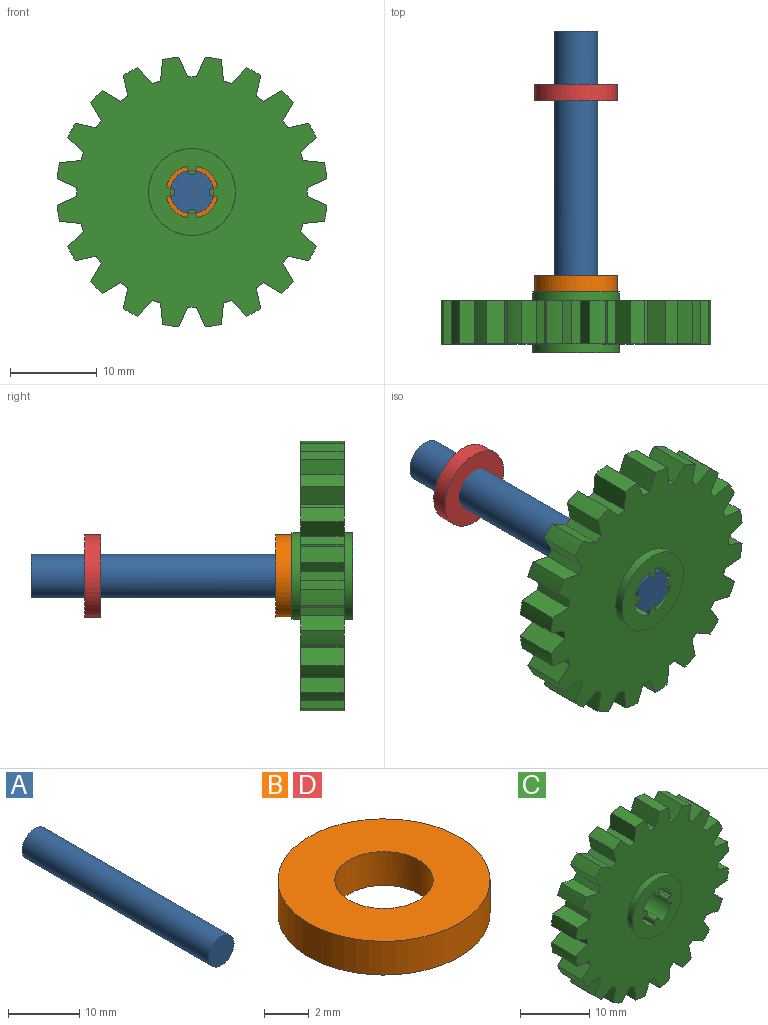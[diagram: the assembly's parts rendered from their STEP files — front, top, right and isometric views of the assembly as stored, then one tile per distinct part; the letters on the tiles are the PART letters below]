
ASSEMBLY  parts=4 mates=5
PART A: 3 faces, bbox 5x37x5 mm
  f0: plane 5x5mm, normal (0,1,0), area 19.6mm2, adj f1
  f1: cylinder r=2.5mm len=37mm, axis (0,-1,0), area 581.2mm2, adj f0,f2
  f2: plane 5x5mm, normal (0,-1,0), area 19.6mm2, adj f1
PART B: 4 faces, bbox 9.5x9.5x1.9 mm
  f0: cylinder r=2.21mm len=4.42mm, axis (0,0,1), area 25.7mm2, adj f1,f3
  f1: plane 9.53x9.53mm, normal (0,0,-1), area 55.9mm2, adj f0,f2
  f2: cylinder r=4.76mm len=9.53mm, axis (0,0,-1), area 55.5mm2, adj f1,f3
  f3: plane 9.53x9.53mm, normal (0,0,1), area 55.9mm2, adj f0,f2
PART C: 102 faces, bbox 31.1x7x31.1 mm
  f0: plane 31.06x31.06mm, normal (0,1,0), area 593.1mm2, adj f1,f7,f8,f9,f10,f11,f12,f13
  f1: cylinder r=5mm len=10mm, axis (0,1,0), area 31.4mm2, adj f0,f2
  f2: plane 10x10mm, normal (0,1,0), area 53.8mm2, adj f1,f3,f87,f88,f89,f90,f91,f92
  f3: cylinder r=0.5mm len=7mm, axis (0,-1,0), area 11mm2, adj f2,f4,f87,f98
  f4: plane 10x10mm, normal (0,-1,0), area 53.8mm2, adj f3,f5,f87,f88,f89,f90,f91,f92
  f5: cylinder r=5mm len=10mm, axis (0,-1,0), area 31.4mm2, adj f4,f6
  f6: plane 31.06x31.06mm, normal (0,-1,0), area 593.1mm2, adj f5,f7,f8,f9,f10,f11,f12,f13
  f7: plane 5x0.95mm, normal (-0.31,0,0.95), area 5mm2, adj f0,f6,f8,f86
  f8: plane 5x2.45mm, normal (-0.99,0,0.1), area 12.3mm2, adj f0,f6,f7,f28
  f9: cylinder r=15.6mm len=5mm, axis (0,-1,0), area 9.5mm2, adj f0,f6,f29,f32
  f10: cylinder r=15.6mm len=5mm, axis (0,-1,0), area 9.5mm2, adj f0,f6,f31,f35
  f11: cylinder r=15.6mm len=5mm, axis (0,-1,0), area 9.5mm2, adj f0,f6,f37,f38
  f12: cylinder r=15.6mm len=5mm, axis (0,-1,0), area 9.5mm2, adj f0,f6,f40,f41
  f13: cylinder r=15.6mm len=5mm, axis (0,-1,0), area 9.5mm2, adj f0,f6,f43,f44
  f14: cylinder r=15.6mm len=5mm, axis (0,-1,0), area 9.5mm2, adj f0,f6,f46,f47
  f15: cylinder r=15.6mm len=5mm, axis (0,-1,0), area 9.5mm2, adj f0,f6,f49,f50
  f16: cylinder r=15.6mm len=5mm, axis (0,-1,0), area 9.5mm2, adj f0,f6,f52,f53
  f17: cylinder r=15.6mm len=5mm, axis (0,-1,0), area 9.5mm2, adj f0,f6,f55,f56
  f18: cylinder r=15.6mm len=5mm, axis (0,-1,0), area 9.5mm2, adj f0,f6,f58,f59
  f19: cylinder r=15.6mm len=5mm, axis (0,-1,0), area 9.5mm2, adj f0,f6,f61,f62
  f20: cylinder r=15.6mm len=5mm, axis (0,-1,0), area 9.5mm2, adj f0,f6,f64,f65
  f21: cylinder r=15.6mm len=5mm, axis (0,-1,0), area 9.5mm2, adj f0,f6,f67,f68
  f22: cylinder r=15.6mm len=5mm, axis (0,-1,0), area 9.5mm2, adj f0,f6,f70,f71
  f23: cylinder r=15.6mm len=5mm, axis (0,-1,0), area 9.5mm2, adj f0,f6,f73,f74
  f24: cylinder r=15.6mm len=5mm, axis (0,-1,0), area 9.5mm2, adj f0,f6,f76,f77
  f25: cylinder r=15.6mm len=5mm, axis (0,-1,0), area 9.5mm2, adj f0,f6,f79,f80
  f26: cylinder r=15.6mm len=5mm, axis (0,-1,0), area 9.5mm2, adj f0,f6,f82,f83
  f27: cylinder r=15.6mm len=5mm, axis (0,-1,0), area 9.5mm2, adj f0,f6,f85,f86
  f28: cylinder r=15.6mm len=5mm, axis (0,-1,0), area 9.5mm2, adj f0,f6,f8,f34
  f29: plane 5x2.45mm, normal (0.99,0,0.1), area 12.3mm2, adj f0,f6,f9,f30
  f30: plane 5x0.95mm, normal (0.31,0,0.95), area 5mm2, adj f0,f6,f29,f31
  f31: plane 5x1.83mm, normal (-0.74,0,0.67), area 12.3mm2, adj f0,f6,f10,f30
  f32: plane 5x2.25mm, normal (-0.91,0,0.41), area 12.3mm2, adj f0,f6,f9,f33
  f33: plane 5x1mm, normal (0,0,1), area 5mm2, adj f0,f6,f32,f34
  f34: plane 5x2.25mm, normal (0.91,0,0.41), area 12.3mm2, adj f0,f6,f28,f33
  f35: plane 5x2.41mm, normal (0.98,0,-0.21), area 12.3mm2, adj f0,f6,f10,f36
  f36: plane 5x0.81mm, normal (0.59,0,0.81), area 5mm2, adj f0,f6,f35,f37
  f37: plane 5x2.13mm, normal (-0.5,0,0.87), area 12.3mm2, adj f0,f6,f11,f36
  f38: plane 5x2.13mm, normal (0.87,0,-0.5), area 12.3mm2, adj f0,f6,f11,f39
  f39: plane 5x0.81mm, normal (0.81,0,0.59), area 5mm2, adj f0,f6,f38,f40
  f40: plane 5x2.41mm, normal (-0.21,0,0.98), area 12.3mm2, adj f0,f6,f12,f39
  f41: plane 5x1.83mm, normal (0.67,0,-0.74), area 12.3mm2, adj f0,f6,f12,f42
  f42: plane 5x0.95mm, normal (0.95,0,0.31), area 5mm2, adj f0,f6,f41,f43
  f43: plane 5x2.45mm, normal (0.1,0,0.99), area 12.3mm2, adj f0,f6,f13,f42
  f44: plane 5x2.25mm, normal (0.41,0,-0.91), area 12.3mm2, adj f0,f6,f13,f45
  f45: plane 5x1mm, normal (1,0,0), area 5mm2, adj f0,f6,f44,f46
  f46: plane 5x2.25mm, normal (0.41,0,0.91), area 12.3mm2, adj f0,f6,f14,f45
  f47: plane 5x2.45mm, normal (0.1,0,-0.99), area 12.3mm2, adj f0,f6,f14,f48
  f48: plane 5x0.95mm, normal (0.95,0,-0.31), area 5mm2, adj f0,f6,f47,f49
  f49: plane 5x1.83mm, normal (0.67,0,0.74), area 12.3mm2, adj f0,f6,f15,f48
  f50: plane 5x2.41mm, normal (-0.21,0,-0.98), area 12.3mm2, adj f0,f6,f15,f51
  f51: plane 5x0.81mm, normal (0.81,0,-0.59), area 5mm2, adj f0,f6,f50,f52
  f52: plane 5x2.13mm, normal (0.87,0,0.5), area 12.3mm2, adj f0,f6,f16,f51
  f53: plane 5x2.13mm, normal (-0.5,0,-0.87), area 12.3mm2, adj f0,f6,f16,f54
  f54: plane 5x0.81mm, normal (0.59,0,-0.81), area 5mm2, adj f0,f6,f53,f55
  f55: plane 5x2.41mm, normal (0.98,0,0.21), area 12.3mm2, adj f0,f6,f17,f54
  f56: plane 5x1.83mm, normal (-0.74,0,-0.67), area 12.3mm2, adj f0,f6,f17,f57
  f57: plane 5x0.95mm, normal (0.31,0,-0.95), area 5mm2, adj f0,f6,f56,f58
  f58: plane 5x2.45mm, normal (0.99,0,-0.1), area 12.3mm2, adj f0,f6,f18,f57
  f59: plane 5x2.25mm, normal (-0.91,0,-0.41), area 12.3mm2, adj f0,f6,f18,f60
  f60: plane 5x1mm, normal (0,0,-1), area 5mm2, adj f0,f6,f59,f61
  f61: plane 5x2.25mm, normal (0.91,0,-0.41), area 12.3mm2, adj f0,f6,f19,f60
  f62: plane 5x2.45mm, normal (-0.99,0,-0.1), area 12.3mm2, adj f0,f6,f19,f63
  f63: plane 5x0.95mm, normal (-0.31,0,-0.95), area 5mm2, adj f0,f6,f62,f64
  f64: plane 5x1.83mm, normal (0.74,0,-0.67), area 12.3mm2, adj f0,f6,f20,f63
  f65: plane 5x2.41mm, normal (-0.98,0,0.21), area 12.3mm2, adj f0,f6,f20,f66
  f66: plane 5x0.81mm, normal (-0.59,0,-0.81), area 5mm2, adj f0,f6,f65,f67
  f67: plane 5x2.13mm, normal (0.5,0,-0.87), area 12.3mm2, adj f0,f6,f21,f66
  f68: plane 5x2.13mm, normal (-0.87,0,0.5), area 12.3mm2, adj f0,f6,f21,f69
  f69: plane 5x0.81mm, normal (-0.81,0,-0.59), area 5mm2, adj f0,f6,f68,f70
  f70: plane 5x2.41mm, normal (0.21,0,-0.98), area 12.3mm2, adj f0,f6,f22,f69
  f71: plane 5x1.83mm, normal (-0.67,0,0.74), area 12.3mm2, adj f0,f6,f22,f72
  f72: plane 5x0.95mm, normal (-0.95,0,-0.31), area 5mm2, adj f0,f6,f71,f73
  f73: plane 5x2.45mm, normal (-0.1,0,-0.99), area 12.3mm2, adj f0,f6,f23,f72
  f74: plane 5x2.25mm, normal (-0.41,0,0.91), area 12.3mm2, adj f0,f6,f23,f75
  f75: plane 5x1mm, normal (-1,0,0), area 5mm2, adj f0,f6,f74,f76
  f76: plane 5x2.25mm, normal (-0.41,0,-0.91), area 12.3mm2, adj f0,f6,f24,f75
  f77: plane 5x2.45mm, normal (-0.1,0,0.99), area 12.3mm2, adj f0,f6,f24,f78
  f78: plane 5x0.95mm, normal (-0.95,0,0.31), area 5mm2, adj f0,f6,f77,f79
  f79: plane 5x1.83mm, normal (-0.67,0,-0.74), area 12.3mm2, adj f0,f6,f25,f78
  f80: plane 5x2.41mm, normal (0.21,0,0.98), area 12.3mm2, adj f0,f6,f25,f81
  f81: plane 5x0.81mm, normal (-0.81,0,0.59), area 5mm2, adj f0,f6,f80,f82
  f82: plane 5x2.13mm, normal (-0.87,0,-0.5), area 12.3mm2, adj f0,f6,f26,f81
  f83: plane 5x2.13mm, normal (0.5,0,0.87), area 12.3mm2, adj f0,f6,f26,f84
  f84: plane 5x0.81mm, normal (-0.59,0,0.81), area 5mm2, adj f0,f6,f83,f85
  f85: plane 5x2.41mm, normal (-0.98,0,-0.21), area 12.3mm2, adj f0,f6,f27,f84
  f86: plane 5x1.83mm, normal (0.74,0,0.67), area 12.3mm2, adj f0,f6,f7,f27
  f87: plane 7x0.46mm, normal (-1,0,0), area 3.2mm2, adj f2,f3,f4,f88
  f88: cylinder r=3mm len=7mm, axis (0,1,0), area 26mm2, adj f2,f4,f87,f92
  f89: cylinder r=3mm len=7mm, axis (0,1,0), area 26mm2, adj f2,f4,f95,f98
  f90: cylinder r=3mm len=7mm, axis (0,1,0), area 26mm2, adj f2,f4,f97,f99
  f91: cylinder r=3mm len=7mm, axis (0,1,0), area 26mm2, adj f2,f4,f94,f101
  f92: plane 7x0.46mm, normal (0,0,1), area 3.2mm2, adj f2,f4,f88,f93
  f93: cylinder r=0.5mm len=7mm, axis (0,-1,0), area 11mm2, adj f2,f4,f92,f94
  f94: plane 7x0.46mm, normal (0,0,-1), area 3.2mm2, adj f2,f4,f91,f93
  f95: plane 7x0.46mm, normal (0,0,1), area 3.2mm2, adj f2,f4,f89,f96
  f96: cylinder r=0.5mm len=7mm, axis (0,-1,0), area 11mm2, adj f2,f4,f95,f97
  f97: plane 7x0.46mm, normal (0,0,-1), area 3.2mm2, adj f2,f4,f90,f96
  f98: plane 7x0.46mm, normal (1,0,0), area 3.2mm2, adj f2,f3,f4,f89
  f99: plane 7x0.46mm, normal (1,0,0), area 3.2mm2, adj f2,f4,f90,f100
  f100: cylinder r=0.5mm len=7mm, axis (0,-1,0), area 11mm2, adj f2,f4,f99,f101
  f101: plane 7x0.46mm, normal (-1,0,0), area 3.2mm2, adj f2,f4,f91,f100
PART D: same geometry as B
PLACE A t=(-31.75,34.58,-15)mm
PLACE B rot(axis=(0,0.71,0.71),180deg) t=(-31.75,4.58,-15)mm
PLACE C t=(-31.75,3.58,-15)mm
PLACE D rot(axis=(0,0.71,0.71),180deg) t=(-31.75,26.59,-15)mm
MATE cylindrical B.f0 <-> C.f1  axis (0,1,0) through (-31.75,6.43,-15)mm
MATE cylindrical D.f0 <-> A.f1  axis (0,-1,0) through (-31.75,26.59,-15)mm
MATE planar B.f0 <-> C.f2  axis (0,-1,0) through (-31.75,4.58,-15)mm
MATE fastened A.f1 <-> C.f1  axis (0,-1,0) through (-31.75,-2.42,-15)mm
MATE cylindrical C.f1 <-> A.f1  axis (0,-1,0) through (-31.75,-1.92,-15)mm
